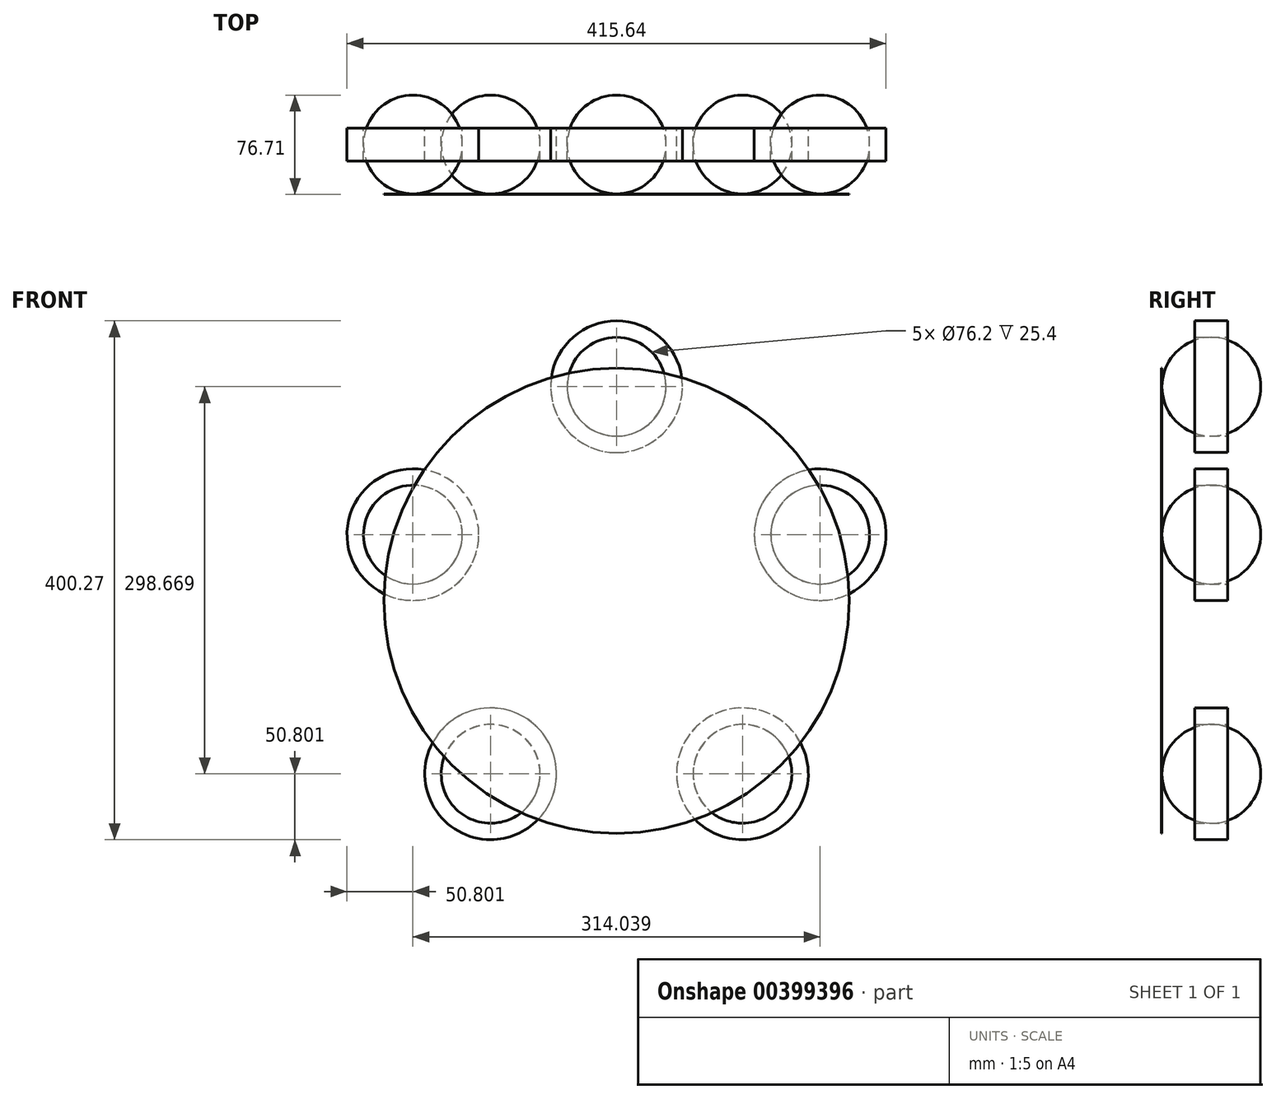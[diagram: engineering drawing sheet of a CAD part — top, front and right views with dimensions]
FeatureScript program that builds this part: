
annotation { "Feature Type Name" : "Feature", "Feature Type Description" : "" }
export const myFeature = defineFeature(function(context is Context, id is Id, definition is map)
    precondition{}
    {
        {
            var Q0;
            Q0=qCreatedBy(makeId("Front.planeOp"),FACE);
            var sketch = newSketch(context, id + "F0", { "sketchPlane" : qUnion([Q0])});
            skCircle(sketch, "E0", {"center": v(0, 0) * mm, "radius": 215.9 * mm, "construction": true});
            skLineSegment(sketch, "E1", {"start": v(0, 215.9) * mm, "end": v(0, -215.9) * mm, "construction": true});
            skCircle(sketch, "E2", {"center": v(0, 165.1) * mm, "radius": 50.8 * mm});
            skCircle(sketch, "E3.1.0", {"center": v(-157.02, 51.02) * mm, "radius": 50.8 * mm});
            skCircle(sketch, "E3.2.0", {"center": v(-97.04, -133.57) * mm, "radius": 50.8 * mm});
            skCircle(sketch, "E3.3.0", {"center": v(97.04, -133.57) * mm, "radius": 50.8 * mm});
            skCircle(sketch, "E3.4.0", {"center": v(157.02, 51.02) * mm, "radius": 50.8 * mm});
            skLineSegment(sketch, "E4", {"start": v(-157.02, 101.82) * mm, "end": v(-157.02, 0.22) * mm, "construction": true});
            skLineSegment(sketch, "E5", {"start": v(-97.04, -82.77) * mm, "end": v(-97.04, -184.37) * mm, "construction": true});
            skLineSegment(sketch, "E6", {"start": v(97.04, -82.77) * mm, "end": v(97.04, -184.37) * mm, "construction": true});
            skLineSegment(sketch, "E7", {"start": v(157.02, 101.82) * mm, "end": v(157.02, 0.22) * mm, "construction": true});
            skCircle(sketch, "E8", {"center": v(0, 165.1) * mm, "radius": 38.1 * mm});
            skCircle(sketch, "E9.1.0", {"center": v(-157.02, 51.02) * mm, "radius": 38.1 * mm});
            skCircle(sketch, "E9.2.0", {"center": v(-97.04, -133.57) * mm, "radius": 38.1 * mm});
            skCircle(sketch, "E9.3.0", {"center": v(97.04, -133.57) * mm, "radius": 38.1 * mm});
            skCircle(sketch, "E9.4.0", {"center": v(157.02, 51.02) * mm, "radius": 38.1 * mm});
            skSolve(sketch);
        }
        {
            var Q0;
            Q0=makeQuery(id+"F0.imprint","IMPRINT",FACE,{"disambiguationData":[TD([[makeQuery(id+"F0.imprint","IMPRINT",EDGE,{"derivedFrom":sQuery(id+"F0.wireOp",EDGE,"E2")}),1.0]])]});
            var Q1;
            Q1=makeQuery(id+"F0.imprint","IMPRINT",FACE,{"disambiguationData":[TD([[makeQuery(id+"F0.imprint","IMPRINT",EDGE,{"derivedFrom":sQuery(id+"F0.wireOp",EDGE,"E3.1.0")}),1.0]])]});
            var Q2;
            Q2=makeQuery(id+"F0.imprint","IMPRINT",FACE,{"disambiguationData":[TD([[makeQuery(id+"F0.imprint","IMPRINT",EDGE,{"derivedFrom":sQuery(id+"F0.wireOp",EDGE,"E3.2.0")}),1.0]])]});
            var Q3;
            Q3=makeQuery(id+"F0.imprint","IMPRINT",FACE,{"disambiguationData":[TD([[makeQuery(id+"F0.imprint","IMPRINT",EDGE,{"derivedFrom":sQuery(id+"F0.wireOp",EDGE,"E3.3.0")}),1.0]])]});
            var Q4;
            Q4=makeQuery(id+"F0.imprint","IMPRINT",FACE,{"disambiguationData":[TD([[makeQuery(id+"F0.imprint","IMPRINT",EDGE,{"derivedFrom":sQuery(id+"F0.wireOp",EDGE,"E3.4.0")}),1.0]])]});
            extrude(context, id + "F1", {"entities" : qUnion([Q0, Q1, Q2, Q3, Q4]), "endBound" : BoundingType.SYMMETRIC, "depth" : 25.4 * mm});
        }
        {
            var Q0;
            Q0=qCreatedBy(makeId("Front.planeOp"),FACE);
            var sketch = newSketch(context, id + "F2", { "sketchPlane" : qUnion([Q0])});
            skArc(sketch, "E10.0", {"start": v(-157.02, 89.12) * mm, "mid": v(-195.12, 51.02) * mm, "end": v(-157.02, 12.92) * mm});
            skLineSegment(sketch, "E11", {"start": v(-157.02, 89.12) * mm, "end": v(-157.02, 12.92) * mm});
            skSolve(sketch);
        }
        {
            var Q0;
            Q0 = qSketchRegion(id + "F2", true);
            var Q1;
            Q1=sQuery(id+"F2.wireOp",EDGE,"E11");
            revolve(context, id + "F3", {"entities" : qUnion([Q0]), "axis" : qUnion([Q1]), "revolveType" : RevolveType.FULL});
        }
        {
            var Q0;
            Q0=qCreatedBy(makeId("Top.planeOp"),FACE);
            var sketch = newSketch(context, id + "F4", { "sketchPlane" : qUnion([Q0])});
            skLineSegment(sketch, "E12", {"start": v(0, 115.5) * mm, "end": v(0, -156.9) * mm, "construction": true});
            skSolve(sketch);
        }
        {
            var Q0;
            Q0=makeQuery(id+"F3.opRevolve","SWEPT_BODY",BODY,{"disambiguationData":[OSD([sQuery(id+"F2.wireOp",EDGE,"E10.0"),sQuery(id+"F2.wireOp",EDGE,"E11")])]});
            var Q1;
            Q1=sQuery(id+"F4.wireOp",EDGE,"E12");
            circularPattern(context, id + "F5", {"entities" : qUnion([Q0]), "axis" : qUnion([Q1]), "angle" : 360 * degree, "instanceCount" : 5, "equalSpace" : true});
        }
        {
            var Q0;
            Q0=qCreatedBy(makeId("Front.planeOp"),FACE);
            cPlane(context, id + "F6", {"entities" : qUnion([Q0]), "cplaneType" : CPlaneType.OFFSET, "offset" : 38.1 * mm, "width" : 152.4 * mm, "height" : 152.4 * mm});
        }
        {
            var Q0;
            Q0=qCreatedBy(id+"F6.planeOp",FACE);
            var sketch = newSketch(context, id + "F7", { "sketchPlane" : qUnion([Q0])});
            skCircle(sketch, "E13", {"center": v(0, 0) * mm, "radius": 179.4 * mm});
            skSolve(sketch);
        }
        {
            var Q0;
            Q0 = qSketchRegion(id + "F7", true);
            extrude(context, id + "F8", {"entities" : qUnion([Q0]), "depth" : 0.5 * mm});
        }
    });
